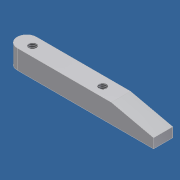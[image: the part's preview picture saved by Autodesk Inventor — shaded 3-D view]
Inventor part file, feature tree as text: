
AUTODESK INVENTOR PART (.ipt)
format: ipt  version: unknown  size: 201,216 bytes
history: native  units: in
note: dims shown in document units (in); Inventor stores cm internally (conversion verified against a paired STEP export)
features: sketch x5, extrude x3, hole x2
ambient origin geometry x8: Origin, YZ Plane, XZ Plane, XY Plane, X Axis, Y Axis, Z Axis, Center Point
bodies: Solid1 (feature_tree)
feature tree (10):
  extrude  "Extrusion1"  Depth=0.313in
  extrude  "Extrusion2"  Depth=1.375in
  hole  "Hole1"  [1 undecoded]
  hole  "Hole2"  [1 undecoded]
  extrude  "Extrusion3"  Depth=0.3125in
  sketch  "Sketch1"  dims[d1=0.625in d2=0.313in]
  sketch  "Sketch2"  dims[d3=4.75in d4=1.375in]
  sketch  "Sketch3"  dims[d5=0.625in d6=0.0in d7=0.313in]
  sketch  "Sketch4"  dims[d8=0.3125in d9=0.625in d10=0.0in]
  sketch  "Sketch5"  dims[d11=1.968in d12=0.3125in d13=0.252in d14=0.75in d15=0.375in d16=0.25in d17=0.5635in d18=1.0in d19=0.8108in d20=2.282in d21=0.3125in d22=0.252in d23=0.75in d24=0.375in d25=0.25in d26=0.5635in d27=1.0in d28=0.8108in d29=0.313in d30=1.0in d31=0.0in]
note: 2 required parameter values undecoded (feature->parameter linkage not recoverable at this tier; creation-order binding heuristic only, values carry confidence <= 0.55)
